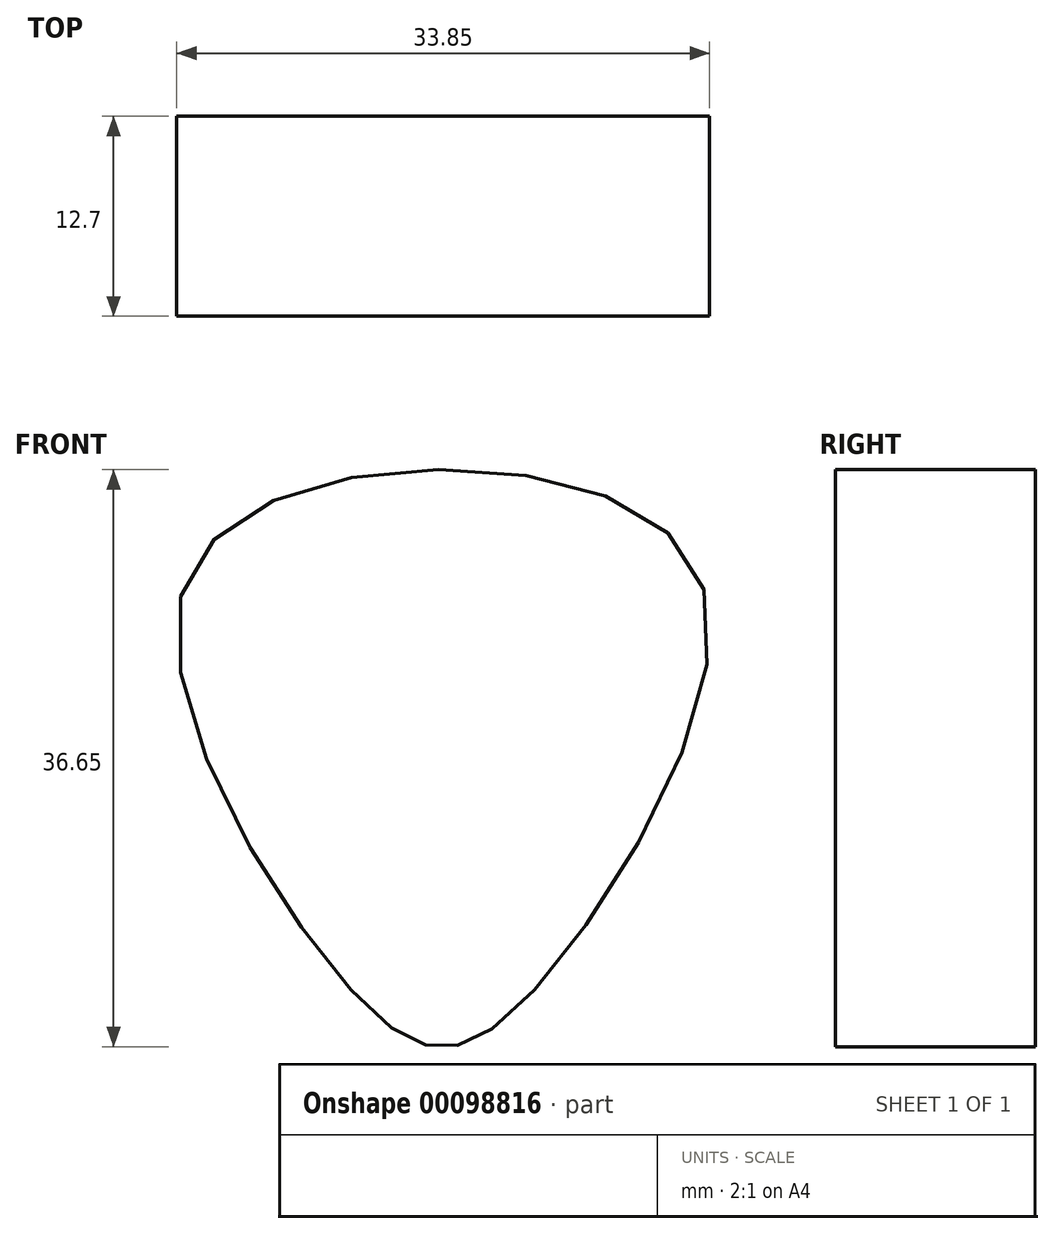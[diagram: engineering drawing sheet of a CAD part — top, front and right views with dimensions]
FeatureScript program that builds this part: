
annotation { "Feature Type Name" : "Feature", "Feature Type Description" : "" }
export const myFeature = defineFeature(function(context is Context, id is Id, definition is map)
    precondition{}
    {
        {
            var Q0;
            Q0=qCreatedBy(makeId("Front.planeOp"),FACE);
            var sketch = newSketch(context, id + "F0", { "sketchPlane" : qUnion([Q0])});
            skFitSpline(sketch, "E0", {"points": [v(-5.64, 3.6) * mm, v(0, 0) * mm, v(5.64, 3.2) * mm, v(16.92, 28.48) * mm, v(0, 36.65) * mm, v(-16.53, 28.3) * mm, v(-5.64, 3.6) * mm]});
            skSolve(sketch);
        }
        {
            var Q0;
            Q0=makeQuery(id+"F0.imprint","IMPRINT",FACE,{"disambiguationData":[TD([[makeQuery(id+"F0.imprint","IMPRINT",EDGE,{"derivedFrom":sQuery(id+"F0.wireOp",EDGE,"E0")}),1.0]])]});
            extrude(context, id + "F1", {"entities" : qUnion([Q0]), "depth" : 12.7 * mm});
        }
    });
